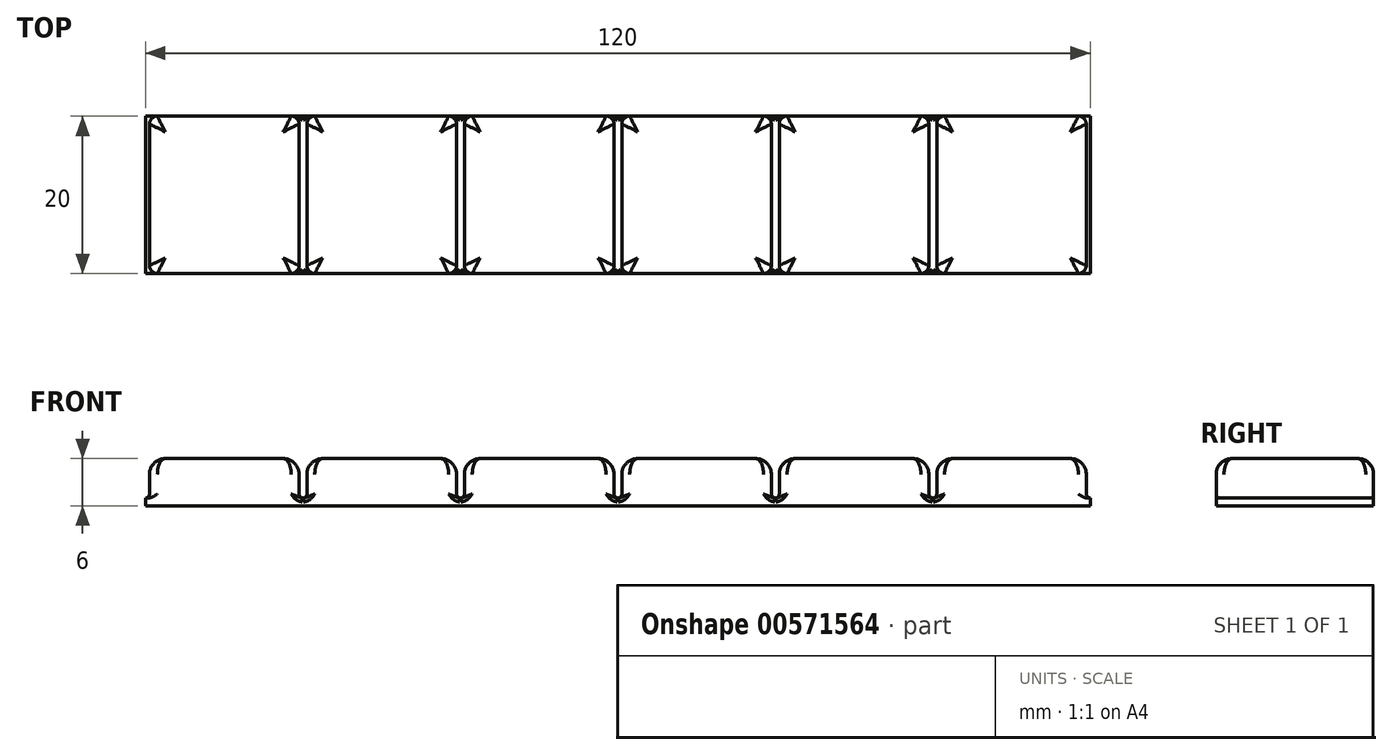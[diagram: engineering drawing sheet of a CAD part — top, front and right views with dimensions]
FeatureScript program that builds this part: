
annotation { "Feature Type Name" : "Feature", "Feature Type Description" : "" }
export const myFeature = defineFeature(function(context is Context, id is Id, definition is map)
    precondition{}
    {
        {
            var Q0;
            Q0=qCreatedBy(makeId("Top.planeOp"),FACE);
            var sketch = newSketch(context, id + "F0", { "sketchPlane" : qUnion([Q0])});
            skLineSegment(sketch, "E0.bottom", {"start": v(60, 10) * mm, "end": v(-60, 10) * mm});
            skLineSegment(sketch, "E0.top", {"start": v(60, -10) * mm, "end": v(-60, -10) * mm});
            skLineSegment(sketch, "E0.left", {"start": v(60, 10) * mm, "end": v(60, -10) * mm});
            skLineSegment(sketch, "E0.right", {"start": v(-60, 10) * mm, "end": v(-60, -10) * mm});
            skPoint(sketch, "E0.middle", {"position": v(0, 0) * mm});
            skPoint(sketch, "E1", {"position": v(-40, -10) * mm});
            skPoint(sketch, "E2", {"position": v(-20, -10) * mm});
            skPoint(sketch, "E3", {"position": v(0, -10) * mm});
            skPoint(sketch, "E4", {"position": v(20, -10) * mm});
            skPoint(sketch, "E5", {"position": v(40, -10) * mm});
            skPoint(sketch, "E6", {"position": v(60, -10) * mm});
            skLineSegment(sketch, "E7", {"start": v(-40, -10) * mm, "end": v(-40, 10) * mm, "construction": true});
            skLineSegment(sketch, "E8", {"start": v(-20, -10) * mm, "end": v(-20, 10) * mm, "construction": true});
            skLineSegment(sketch, "E9", {"start": v(0, -10) * mm, "end": v(0, 10) * mm, "construction": true});
            skLineSegment(sketch, "E10", {"start": v(20, 10) * mm, "end": v(20, -10) * mm, "construction": true});
            skLineSegment(sketch, "E11", {"start": v(40, -10) * mm, "end": v(40, 10) * mm, "construction": true});
            skLineSegment(sketch, "E12.0", {"start": v(-59.5, 10) * mm, "end": v(-59.5, -10) * mm});
            skLineSegment(sketch, "E13.0", {"start": v(-39.5, -10) * mm, "end": v(-39.5, 10) * mm});
            skLineSegment(sketch, "E14.0", {"start": v(-40.5, -10) * mm, "end": v(-40.5, 10) * mm});
            skLineSegment(sketch, "E15.0", {"start": v(-20.5, -10) * mm, "end": v(-20.5, 10) * mm});
            skLineSegment(sketch, "E16.0", {"start": v(-19.5, -10) * mm, "end": v(-19.5, 10) * mm});
            skLineSegment(sketch, "E17.0", {"start": v(0.5, -10) * mm, "end": v(0.5, 10) * mm});
            skLineSegment(sketch, "E18.0", {"start": v(-0.5, -10) * mm, "end": v(-0.5, 10) * mm});
            skLineSegment(sketch, "E19.0", {"start": v(19.5, 10) * mm, "end": v(19.5, -10) * mm});
            skLineSegment(sketch, "E20.0", {"start": v(20.5, 10) * mm, "end": v(20.5, -10) * mm});
            skLineSegment(sketch, "E21.0", {"start": v(40.5, -10) * mm, "end": v(40.5, 10) * mm});
            skLineSegment(sketch, "E22.0", {"start": v(59.5, 10) * mm, "end": v(59.5, -10) * mm});
            skLineSegment(sketch, "E23.0", {"start": v(39.5, -10) * mm, "end": v(39.5, 10) * mm});
            skSolve(sketch);
        }
        {
            var Q0;
            {var subQ0=sQuery(id+"F0.wireOp",EDGE,"E0.right");Q0=makeQuery(id+"F0.imprint","IMPRINT",FACE,{"disambiguationData":[TD([[makeQuery(id+"F0.imprint","IMPRINT",EDGE,{"derivedFrom":subQ0}),1.0]])]});}
            var Q1;
            {var subQ0=sQuery(id+"F0.wireOp",EDGE,"E12.0");Q1=makeQuery(id+"F0.imprint","IMPRINT",FACE,{"disambiguationData":[TD([[makeQuery(id+"F0.imprint","IMPRINT",EDGE,{"derivedFrom":subQ0}),1.0]])]});}
            var Q2;
            {var subQ0=sQuery(id+"F0.wireOp",EDGE,"E13.0");Q2=makeQuery(id+"F0.imprint","IMPRINT",FACE,{"disambiguationData":[TD([[makeQuery(id+"F0.imprint","IMPRINT",EDGE,{"derivedFrom":subQ0}),1.0]])]});}
            var Q3;
            {var subQ0=sQuery(id+"F0.wireOp",EDGE,"E13.0");Q3=makeQuery(id+"F0.imprint","IMPRINT",FACE,{"disambiguationData":[TD([[makeQuery(id+"F0.imprint","IMPRINT",EDGE,{"derivedFrom":subQ0}),-1.0]])]});}
            var Q4;
            {var subQ0=sQuery(id+"F0.wireOp",EDGE,"E15.0");Q4=makeQuery(id+"F0.imprint","IMPRINT",FACE,{"disambiguationData":[TD([[makeQuery(id+"F0.imprint","IMPRINT",EDGE,{"derivedFrom":subQ0}),-1.0]])]});}
            var Q5;
            {var subQ0=sQuery(id+"F0.wireOp",EDGE,"E16.0");Q5=makeQuery(id+"F0.imprint","IMPRINT",FACE,{"disambiguationData":[TD([[makeQuery(id+"F0.imprint","IMPRINT",EDGE,{"derivedFrom":subQ0}),-1.0]])]});}
            var Q6;
            {var subQ0=sQuery(id+"F0.wireOp",EDGE,"E17.0");Q6=makeQuery(id+"F0.imprint","IMPRINT",FACE,{"disambiguationData":[TD([[makeQuery(id+"F0.imprint","IMPRINT",EDGE,{"derivedFrom":subQ0}),1.0]])]});}
            var Q7;
            {var subQ0=sQuery(id+"F0.wireOp",EDGE,"E19.0");Q7=makeQuery(id+"F0.imprint","IMPRINT",FACE,{"disambiguationData":[TD([[makeQuery(id+"F0.imprint","IMPRINT",EDGE,{"derivedFrom":subQ0}),1.0]])]});}
            var Q8;
            {var subQ0=sQuery(id+"F0.wireOp",EDGE,"E21.0");Q8=makeQuery(id+"F0.imprint","IMPRINT",FACE,{"disambiguationData":[TD([[makeQuery(id+"F0.imprint","IMPRINT",EDGE,{"derivedFrom":subQ0}),1.0]])]});}
            var Q9;
            {var subQ0=sQuery(id+"F0.wireOp",EDGE,"E0.left");Q9=makeQuery(id+"F0.imprint","IMPRINT",FACE,{"disambiguationData":[TD([[makeQuery(id+"F0.imprint","IMPRINT",EDGE,{"derivedFrom":subQ0}),-1.0]])]});}
            var Q10;
            {var subQ0=sQuery(id+"F0.wireOp",EDGE,"E21.0");Q10=makeQuery(id+"F0.imprint","IMPRINT",FACE,{"disambiguationData":[TD([[makeQuery(id+"F0.imprint","IMPRINT",EDGE,{"derivedFrom":subQ0}),-1.0]])]});}
            var Q11;
            {var subQ0=sQuery(id+"F0.wireOp",EDGE,"E20.0");Q11=makeQuery(id+"F0.imprint","IMPRINT",FACE,{"disambiguationData":[TD([[makeQuery(id+"F0.imprint","IMPRINT",EDGE,{"derivedFrom":subQ0}),1.0]])]});}
            var Q12;
            {var subQ0=sQuery(id+"F0.wireOp",EDGE,"E17.0");Q12=makeQuery(id+"F0.imprint","IMPRINT",FACE,{"disambiguationData":[TD([[makeQuery(id+"F0.imprint","IMPRINT",EDGE,{"derivedFrom":subQ0}),-1.0]])]});}
            extrude(context, id + "F1", {"entities" : qUnion([Q0, Q1, Q2, Q3, Q4, Q5, Q6, Q7, Q8, Q9, Q10, Q11, Q12]), "depth" : 1 * mm, "offsetDistance" : 25 * mm});
        }
        {
            var Q0;
            {var subQ0=sQuery(id+"F0.wireOp",EDGE,"E12.0");Q0=makeQuery(id+"F0.imprint","IMPRINT",FACE,{"disambiguationData":[TD([[makeQuery(id+"F0.imprint","IMPRINT",EDGE,{"derivedFrom":subQ0}),1.0]])]});}
            var Q1;
            {var subQ0=sQuery(id+"F0.wireOp",EDGE,"E13.0");Q1=makeQuery(id+"F0.imprint","IMPRINT",FACE,{"disambiguationData":[TD([[makeQuery(id+"F0.imprint","IMPRINT",EDGE,{"derivedFrom":subQ0}),-1.0]])]});}
            var Q2;
            {var subQ0=sQuery(id+"F0.wireOp",EDGE,"E16.0");Q2=makeQuery(id+"F0.imprint","IMPRINT",FACE,{"disambiguationData":[TD([[makeQuery(id+"F0.imprint","IMPRINT",EDGE,{"derivedFrom":subQ0}),-1.0]])]});}
            var Q3;
            {var subQ0=sQuery(id+"F0.wireOp",EDGE,"E17.0");Q3=makeQuery(id+"F0.imprint","IMPRINT",FACE,{"disambiguationData":[TD([[makeQuery(id+"F0.imprint","IMPRINT",EDGE,{"derivedFrom":subQ0}),-1.0]])]});}
            var Q4;
            {var subQ0=sQuery(id+"F0.wireOp",EDGE,"E20.0");Q4=makeQuery(id+"F0.imprint","IMPRINT",FACE,{"disambiguationData":[TD([[makeQuery(id+"F0.imprint","IMPRINT",EDGE,{"derivedFrom":subQ0}),1.0]])]});}
            var Q5;
            {var subQ0=sQuery(id+"F0.wireOp",EDGE,"E21.0");Q5=makeQuery(id+"F0.imprint","IMPRINT",FACE,{"disambiguationData":[TD([[makeQuery(id+"F0.imprint","IMPRINT",EDGE,{"derivedFrom":subQ0}),-1.0]])]});}
            extrude(context, id + "F2", {"entities" : qUnion([Q0, Q1, Q2, Q3, Q4, Q5]), "operationType" : NewBodyOperationType.ADD, "depth" : 6 * mm, "offsetDistance" : 25 * mm});
        }
        {
            var Q0;
            Q0=makeQuery(id+"F2.opExtrude","CAP_FACE",FACE,{"disambiguationData":[OSD([sQuery(id+"F0.wireOp",EDGE,"E0.bottom"),sQuery(id+"F0.wireOp",EDGE,"E0.top"),sQuery(id+"F0.wireOp",EDGE,"E21.0"),sQuery(id+"F0.wireOp",EDGE,"E22.0")])],"isStart":false});
            var Q1;
            Q1=makeQuery(id+"F2.opExtrude","CAP_FACE",FACE,{"disambiguationData":[OSD([sQuery(id+"F0.wireOp",EDGE,"E0.bottom"),sQuery(id+"F0.wireOp",EDGE,"E0.top"),sQuery(id+"F0.wireOp",EDGE,"E20.0"),sQuery(id+"F0.wireOp",EDGE,"E23.0")])],"isStart":false});
            var Q2;
            Q2=makeQuery(id+"F2.opExtrude","CAP_FACE",FACE,{"disambiguationData":[OSD([sQuery(id+"F0.wireOp",EDGE,"E0.bottom"),sQuery(id+"F0.wireOp",EDGE,"E0.top"),sQuery(id+"F0.wireOp",EDGE,"E17.0"),sQuery(id+"F0.wireOp",EDGE,"E19.0")])],"isStart":false});
            var Q3;
            Q3=makeQuery(id+"F2.opExtrude","CAP_FACE",FACE,{"disambiguationData":[OSD([sQuery(id+"F0.wireOp",EDGE,"E0.bottom"),sQuery(id+"F0.wireOp",EDGE,"E0.top"),sQuery(id+"F0.wireOp",EDGE,"E16.0"),sQuery(id+"F0.wireOp",EDGE,"E18.0")])],"isStart":false});
            var Q4;
            Q4=makeQuery(id+"F2.opExtrude","CAP_FACE",FACE,{"disambiguationData":[OSD([sQuery(id+"F0.wireOp",EDGE,"E0.bottom"),sQuery(id+"F0.wireOp",EDGE,"E0.top"),sQuery(id+"F0.wireOp",EDGE,"E13.0"),sQuery(id+"F0.wireOp",EDGE,"E15.0")])],"isStart":false});
            var Q5;
            Q5=makeQuery(id+"F2.opExtrude","CAP_FACE",FACE,{"disambiguationData":[OSD([sQuery(id+"F0.wireOp",EDGE,"E0.bottom"),sQuery(id+"F0.wireOp",EDGE,"E0.top"),sQuery(id+"F0.wireOp",EDGE,"E12.0"),sQuery(id+"F0.wireOp",EDGE,"E14.0")])],"isStart":false});
            fillet(context, id + "F3", {"entities" : qUnion([Q0, Q1, Q2, Q3, Q4, Q5]), "radius" : 2 * mm, "tangentPropagation" : true, "allowEdgeOverflow" : false});
        }
        {
            var Q0;
            Q0=makeQuery(id+"F2.opExtrude","SWEPT_EDGE",EDGE,{"disambiguationData":[OSD([sQuery(id+"F0.wireOp",EDGE,"E0.bottom"),sQuery(id+"F0.wireOp",EDGE,"E12.0")])]});
            var Q1;
            Q1=makeQuery(id+"F2.opExtrude","SWEPT_EDGE",EDGE,{"disambiguationData":[OSD([sQuery(id+"F0.wireOp",EDGE,"E0.bottom"),sQuery(id+"F0.wireOp",EDGE,"E14.0")])]});
            var Q2;
            Q2=makeQuery(id+"F2.opExtrude","SWEPT_EDGE",EDGE,{"disambiguationData":[OSD([sQuery(id+"F0.wireOp",EDGE,"E0.bottom"),sQuery(id+"F0.wireOp",EDGE,"E13.0")])]});
            var Q3;
            Q3=makeQuery(id+"F2.opExtrude","SWEPT_EDGE",EDGE,{"disambiguationData":[OSD([sQuery(id+"F0.wireOp",EDGE,"E0.bottom"),sQuery(id+"F0.wireOp",EDGE,"E15.0")])]});
            var Q4;
            Q4=makeQuery(id+"F2.opExtrude","SWEPT_EDGE",EDGE,{"disambiguationData":[OSD([sQuery(id+"F0.wireOp",EDGE,"E0.bottom"),sQuery(id+"F0.wireOp",EDGE,"E16.0")])]});
            var Q5;
            Q5=makeQuery(id+"F2.opExtrude","SWEPT_EDGE",EDGE,{"disambiguationData":[OSD([sQuery(id+"F0.wireOp",EDGE,"E0.bottom"),sQuery(id+"F0.wireOp",EDGE,"E18.0")])]});
            var Q6;
            Q6=makeQuery(id+"F2.opExtrude","SWEPT_EDGE",EDGE,{"disambiguationData":[OSD([sQuery(id+"F0.wireOp",EDGE,"E0.bottom"),sQuery(id+"F0.wireOp",EDGE,"E17.0")])]});
            var Q7;
            Q7=makeQuery(id+"F2.opExtrude","SWEPT_EDGE",EDGE,{"disambiguationData":[OSD([sQuery(id+"F0.wireOp",EDGE,"E0.bottom"),sQuery(id+"F0.wireOp",EDGE,"E19.0")])]});
            var Q8;
            Q8=makeQuery(id+"F2.opExtrude","SWEPT_EDGE",EDGE,{"disambiguationData":[OSD([sQuery(id+"F0.wireOp",EDGE,"E0.bottom"),sQuery(id+"F0.wireOp",EDGE,"E20.0")])]});
            var Q9;
            Q9=makeQuery(id+"F2.opExtrude","SWEPT_EDGE",EDGE,{"disambiguationData":[OSD([sQuery(id+"F0.wireOp",EDGE,"E0.bottom"),sQuery(id+"F0.wireOp",EDGE,"E23.0")])]});
            var Q10;
            Q10=makeQuery(id+"F2.opExtrude","SWEPT_EDGE",EDGE,{"disambiguationData":[OSD([sQuery(id+"F0.wireOp",EDGE,"E0.bottom"),sQuery(id+"F0.wireOp",EDGE,"E21.0")])]});
            var Q11;
            Q11=makeQuery(id+"F2.opExtrude","SWEPT_EDGE",EDGE,{"disambiguationData":[OSD([sQuery(id+"F0.wireOp",EDGE,"E0.bottom"),sQuery(id+"F0.wireOp",EDGE,"E22.0")])]});
            var Q12;
            Q12=makeQuery(id+"F2.opExtrude","SWEPT_EDGE",EDGE,{"disambiguationData":[OSD([sQuery(id+"F0.wireOp",EDGE,"E0.top"),sQuery(id+"F0.wireOp",EDGE,"E22.0")])]});
            var Q13;
            Q13=makeQuery(id+"F2.opExtrude","SWEPT_EDGE",EDGE,{"disambiguationData":[OSD([sQuery(id+"F0.wireOp",EDGE,"E0.top"),sQuery(id+"F0.wireOp",EDGE,"E23.0")])]});
            var Q14;
            Q14=makeQuery(id+"F2.opExtrude","SWEPT_EDGE",EDGE,{"disambiguationData":[OSD([sQuery(id+"F0.wireOp",EDGE,"E0.top"),sQuery(id+"F0.wireOp",EDGE,"E19.0")])]});
            var Q15;
            Q15=makeQuery(id+"F2.opExtrude","SWEPT_EDGE",EDGE,{"disambiguationData":[OSD([sQuery(id+"F0.wireOp",EDGE,"E0.top"),sQuery(id+"F0.wireOp",EDGE,"E15.0")])]});
            var Q16;
            Q16=makeQuery(id+"F2.opExtrude","SWEPT_EDGE",EDGE,{"disambiguationData":[OSD([sQuery(id+"F0.wireOp",EDGE,"E0.top"),sQuery(id+"F0.wireOp",EDGE,"E21.0")])]});
            var Q17;
            Q17=makeQuery(id+"F2.opExtrude","SWEPT_EDGE",EDGE,{"disambiguationData":[OSD([sQuery(id+"F0.wireOp",EDGE,"E0.top"),sQuery(id+"F0.wireOp",EDGE,"E20.0")])]});
            var Q18;
            Q18=makeQuery(id+"F2.opExtrude","SWEPT_EDGE",EDGE,{"disambiguationData":[OSD([sQuery(id+"F0.wireOp",EDGE,"E0.top"),sQuery(id+"F0.wireOp",EDGE,"E17.0")])]});
            var Q19;
            Q19=makeQuery(id+"F2.opExtrude","SWEPT_EDGE",EDGE,{"disambiguationData":[OSD([sQuery(id+"F0.wireOp",EDGE,"E0.top"),sQuery(id+"F0.wireOp",EDGE,"E18.0")])]});
            var Q20;
            Q20=makeQuery(id+"F2.opExtrude","SWEPT_EDGE",EDGE,{"disambiguationData":[OSD([sQuery(id+"F0.wireOp",EDGE,"E0.top"),sQuery(id+"F0.wireOp",EDGE,"E16.0")])]});
            var Q21;
            Q21=makeQuery(id+"F2.opExtrude","SWEPT_EDGE",EDGE,{"disambiguationData":[OSD([sQuery(id+"F0.wireOp",EDGE,"E0.top"),sQuery(id+"F0.wireOp",EDGE,"E13.0")])]});
            var Q22;
            Q22=makeQuery(id+"F2.opExtrude","SWEPT_EDGE",EDGE,{"disambiguationData":[OSD([sQuery(id+"F0.wireOp",EDGE,"E0.top"),sQuery(id+"F0.wireOp",EDGE,"E14.0")])]});
            var Q23;
            Q23=makeQuery(id+"F2.opExtrude","SWEPT_EDGE",EDGE,{"disambiguationData":[OSD([sQuery(id+"F0.wireOp",EDGE,"E0.top"),sQuery(id+"F0.wireOp",EDGE,"E12.0")])]});
            fillet(context, id + "F4", {"entities" : qUnion([Q0, Q1, Q2, Q3, Q4, Q5, Q6, Q7, Q8, Q9, Q10, Q11, Q12, Q13, Q14, Q15, Q16, Q17, Q18, Q19, Q20, Q21, Q22, Q23]), "radius" : 1 * mm, "tangentPropagation" : true, "allowEdgeOverflow" : false});
        }
        {
            var Q0;
            Q0=makeQuery(id+"F2.boolean.opBoolean","INTERSECT",EDGE,{"derivedFrom":[makeQuery(id+"F1.opExtrude","CAP_FACE",FACE,{"disambiguationData":[OSD([sQuery(id+"F0.wireOp",EDGE,"E0.bottom"),sQuery(id+"F0.wireOp",EDGE,"E0.top"),sQuery(id+"F0.wireOp",EDGE,"E0.left"),sQuery(id+"F0.wireOp",EDGE,"E0.right")])],"isStart":false}),makeQuery(id+"F2.opExtrude","SWEPT_FACE",FACE,{"disambiguationData":[OSD([sQuery(id+"F0.wireOp",EDGE,"E22.0")])]})]});
            var Q1;
            {var subQ1=sQuery(id+"F0.wireOp",EDGE,"E0.top");var subQ4=sQuery(id+"F0.wireOp",EDGE,"E0.bottom");var subQ12=sQuery(id+"F0.wireOp",EDGE,"E21.0");Q1=makeQuery(id+"F2.boolean.opBoolean","SPLIT",FACE,{"disambiguationData":[TD([makeQuery(id+"F2.opExtrude","SWEPT_FACE",FACE,{"disambiguationData":[OSD([subQ12])]})])],"derivedFrom":makeQuery(id+"F1.opExtrude","CAP_FACE",FACE,{"disambiguationData":[OSD([subQ4,subQ1,sQuery(id+"F0.wireOp",EDGE,"E0.left"),sQuery(id+"F0.wireOp",EDGE,"E0.right")])],"isStart":false})});}
            var Q2;
            {var subQ1=sQuery(id+"F0.wireOp",EDGE,"E0.top");var subQ4=sQuery(id+"F0.wireOp",EDGE,"E0.bottom");var subQ11=sQuery(id+"F0.wireOp",EDGE,"E19.0");Q2=makeQuery(id+"F2.boolean.opBoolean","SPLIT",FACE,{"disambiguationData":[TD([makeQuery(id+"F2.opExtrude","SWEPT_FACE",FACE,{"disambiguationData":[OSD([subQ11])]})])],"derivedFrom":makeQuery(id+"F1.opExtrude","CAP_FACE",FACE,{"disambiguationData":[OSD([subQ4,subQ1,sQuery(id+"F0.wireOp",EDGE,"E0.left"),sQuery(id+"F0.wireOp",EDGE,"E0.right")])],"isStart":false})});}
            var Q3;
            {var subQ1=sQuery(id+"F0.wireOp",EDGE,"E0.top");var subQ4=sQuery(id+"F0.wireOp",EDGE,"E0.bottom");var subQ10=sQuery(id+"F0.wireOp",EDGE,"E17.0");Q3=makeQuery(id+"F2.boolean.opBoolean","SPLIT",FACE,{"disambiguationData":[TD([makeQuery(id+"F2.opExtrude","SWEPT_FACE",FACE,{"disambiguationData":[OSD([subQ10])]})])],"derivedFrom":makeQuery(id+"F1.opExtrude","CAP_FACE",FACE,{"disambiguationData":[OSD([subQ4,subQ1,sQuery(id+"F0.wireOp",EDGE,"E0.left"),sQuery(id+"F0.wireOp",EDGE,"E0.right")])],"isStart":false})});}
            var Q4;
            {var subQ1=sQuery(id+"F0.wireOp",EDGE,"E0.top");var subQ4=sQuery(id+"F0.wireOp",EDGE,"E0.bottom");var subQ7=sQuery(id+"F0.wireOp",EDGE,"E15.0");Q4=makeQuery(id+"F2.boolean.opBoolean","SPLIT",FACE,{"disambiguationData":[TD([makeQuery(id+"F2.opExtrude","SWEPT_FACE",FACE,{"disambiguationData":[OSD([subQ7])]})])],"derivedFrom":makeQuery(id+"F1.opExtrude","CAP_FACE",FACE,{"disambiguationData":[OSD([subQ4,subQ1,sQuery(id+"F0.wireOp",EDGE,"E0.left"),sQuery(id+"F0.wireOp",EDGE,"E0.right")])],"isStart":false})});}
            var Q5;
            {var subQ1=sQuery(id+"F0.wireOp",EDGE,"E0.top");var subQ4=sQuery(id+"F0.wireOp",EDGE,"E0.bottom");var subQ6=sQuery(id+"F0.wireOp",EDGE,"E13.0");Q5=makeQuery(id+"F2.boolean.opBoolean","SPLIT",FACE,{"disambiguationData":[TD([makeQuery(id+"F2.opExtrude","SWEPT_FACE",FACE,{"disambiguationData":[OSD([subQ6])]})])],"derivedFrom":makeQuery(id+"F1.opExtrude","CAP_FACE",FACE,{"disambiguationData":[OSD([subQ4,subQ1,sQuery(id+"F0.wireOp",EDGE,"E0.left"),sQuery(id+"F0.wireOp",EDGE,"E0.right")])],"isStart":false})});}
            var Q6;
            Q6=makeQuery(id+"F2.boolean.opBoolean","INTERSECT",EDGE,{"derivedFrom":[makeQuery(id+"F1.opExtrude","CAP_FACE",FACE,{"disambiguationData":[OSD([sQuery(id+"F0.wireOp",EDGE,"E0.bottom"),sQuery(id+"F0.wireOp",EDGE,"E0.top"),sQuery(id+"F0.wireOp",EDGE,"E0.left"),sQuery(id+"F0.wireOp",EDGE,"E0.right")])],"isStart":false}),makeQuery(id+"F2.opExtrude","SWEPT_FACE",FACE,{"disambiguationData":[OSD([sQuery(id+"F0.wireOp",EDGE,"E12.0")])]})]});
            fillet(context, id + "F5", {"entities" : qUnion([Q0, Q1, Q2, Q3, Q4, Q5, Q6]), "radius" : .5 * mm, "tangentPropagation" : true, "allowEdgeOverflow" : false});
        }
    });
